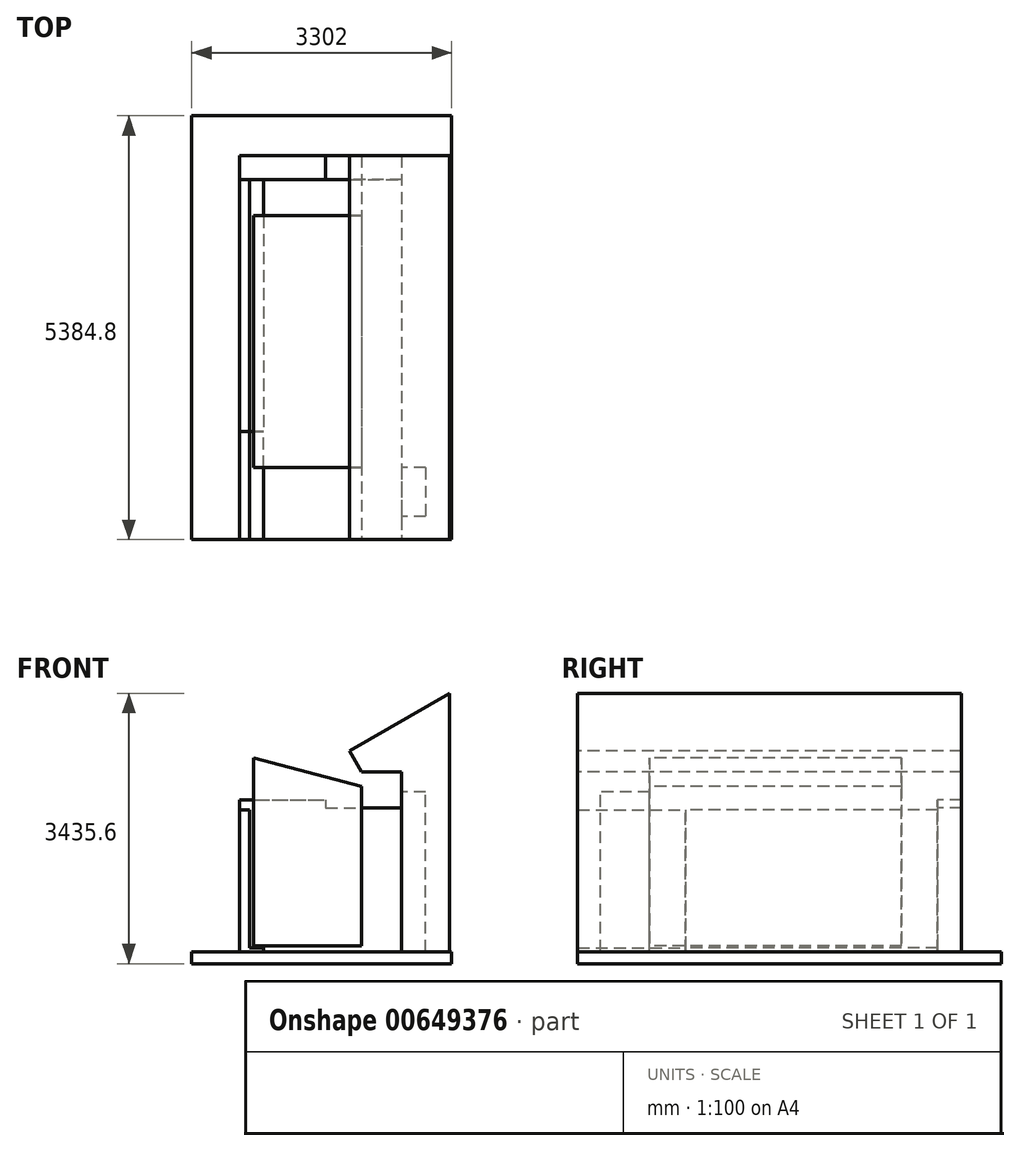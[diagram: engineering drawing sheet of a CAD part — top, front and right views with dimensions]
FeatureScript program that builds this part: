
annotation { "Feature Type Name" : "Feature", "Feature Type Description" : "" }
export const myFeature = defineFeature(function(context is Context, id is Id, definition is map)
    precondition{}
    {
        {
            var Q0;
            Q0=qCreatedBy(makeId("Front.planeOp"),FACE);
            var sketch = newSketch(context, id + "F0", { "sketchPlane" : qUnion([Q0])});
            skLineSegment(sketch, "E0", {"start": v(0, 0) * mm, "end": v(0, 1803.4) * mm});
            skLineSegment(sketch, "E1", {"start": v(0, 1803.4) * mm, "end": v(127, 1803.4) * mm});
            skLineSegment(sketch, "E2", {"start": v(127, 1803.4) * mm, "end": v(127, 50.8) * mm});
            skLineSegment(sketch, "E3", {"start": v(127, 50.8) * mm, "end": v(304.8, 50.8) * mm});
            skLineSegment(sketch, "E4", {"start": v(304.8, 50.8) * mm, "end": v(304.8, 0) * mm});
            skLineSegment(sketch, "E5", {"start": v(304.8, 0) * mm, "end": v(0, 0) * mm});
            skSolve(sketch);
        }
        {
            var Q0;
            Q0=makeQuery(id+"F0.imprint","IMPRINT",FACE,{"disambiguationData":[TD([[makeQuery(id+"F0.imprint","IMPRINT",EDGE,{"derivedFrom":sQuery(id+"F0.wireOp",EDGE,"E0")}),-1.0]])]});
            extrude(context, id + "F1", {"entities" : qUnion([Q0]), "oppositeDirection" : true, "depth" : 3200.4 * mm, "offsetDistance" : 25.4 * mm});
        }
        {
            var Q0;
            Q0=qCreatedBy(makeId("Front.planeOp"),FACE);
            var sketch = newSketch(context, id + "F2", { "sketchPlane" : qUnion([Q0])});
            skLineSegment(sketch, "E6", {"start": v(2057.4, 0) * mm, "end": v(2057.4, 2286) * mm});
            skLineSegment(sketch, "E7", {"start": v(2057.4, 2286) * mm, "end": v(1549.4, 2286) * mm});
            skLineSegment(sketch, "E8", {"start": v(1549.4, 2286) * mm, "end": v(1397, 2549.96) * mm});
            skLineSegment(sketch, "E9", {"start": v(1397, 2549.96) * mm, "end": v(2667, 3283.2) * mm});
            skLineSegment(sketch, "E10", {"start": v(2667, 3283.2) * mm, "end": v(2667, 0) * mm});
            skLineSegment(sketch, "E11", {"start": v(2667, 0) * mm, "end": v(2057.4, 0) * mm});
            skSolve(sketch);
        }
        {
            var Q0;
            Q0 = qSketchRegion(id + "F2", true);
            extrude(context, id + "F3", {"entities" : qUnion([Q0]), "oppositeDirection" : true, "depth" : 3505.2 * mm, "offsetDistance" : 25.4 * mm});
        }
        {
            var Q0;
            Q0=makeQuery(id+"F1.opExtrude","CAP_FACE",FACE,{"disambiguationData":[OSD([sQuery(id+"F0.wireOp",EDGE,"E0"),sQuery(id+"F0.wireOp",EDGE,"E1"),sQuery(id+"F0.wireOp",EDGE,"E2"),sQuery(id+"F0.wireOp",EDGE,"E3"),sQuery(id+"F0.wireOp",EDGE,"E4"),sQuery(id+"F0.wireOp",EDGE,"E5")])],"isStart":false});
            var sketch = newSketch(context, id + "F4", { "sketchPlane" : qUnion([Q0])});
            skLineSegment(sketch, "E12", {"start": v(0, 0) * mm, "end": v(0, 1930.4) * mm});
            skLineSegment(sketch, "E13", {"start": v(0, 1930.4) * mm, "end": v(-1092.2, 1930.4) * mm});
            skLineSegment(sketch, "E14", {"start": v(-1092.2, 1930.4) * mm, "end": v(-1092.2, 1828.8) * mm});
            skLineSegment(sketch, "E15", {"start": v(-1092.2, 1828.8) * mm, "end": v(-2057.4, 1828.8) * mm});
            skLineSegment(sketch, "E16", {"start": v(-2057.4, 1828.8) * mm, "end": v(-2057.4, 0) * mm});
            skLineSegment(sketch, "E17", {"start": v(-2057.4, 0) * mm, "end": v(0, 0) * mm});
            skSolve(sketch);
        }
        {
            var Q0;
            Q0 = qSketchRegion(id + "F4", true);
            extrude(context, id + "F5", {"entities" : qUnion([Q0]), "depth" : 304.8 * mm, "offsetDistance" : 25.4 * mm});
        }
        {
            var Q0;
            Q0=qCreatedBy(makeId("Front.planeOp"),FACE);
            cPlane(context, id + "F6", {"entities" : qUnion([Q0]), "cplaneType" : CPlaneType.OFFSET, "offset" : 1371.6 * mm, "width" : 152.4 * mm, "height" : 152.4 * mm});
        }
        {
            var Q0;
            Q0=makeQuery(id+"F3.opExtrude","CAP_FACE",FACE,{"disambiguationData":[OSD([sQuery(id+"F2.wireOp",EDGE,"E6"),sQuery(id+"F2.wireOp",EDGE,"E7"),sQuery(id+"F2.wireOp",EDGE,"E8"),sQuery(id+"F2.wireOp",EDGE,"E9"),sQuery(id+"F2.wireOp",EDGE,"E10"),sQuery(id+"F2.wireOp",EDGE,"E11")])],"isStart":true});
            var sketch = newSketch(context, id + "F7", { "sketchPlane" : qUnion([Q0])});
            skSolve(sketch);
        }
        {
            var Q0;
            Q0=makeQuery(id+"F7.imprint","IMPRINT",FACE,{"disambiguationData":[TD([[makeQuery(id+"F7.imprint","IMPRINT",EDGE,{"derivedFrom":makeQuery(id+"F3.opExtrude","CAP_EDGE",EDGE,{"disambiguationData":[OSD([sQuery(id+"F2.wireOp",EDGE,"E6")])],"isStart":true})}),-1.0]])]});
            var Q1;
            Q1=qCreatedBy(id+"F6.planeOp",FACE);
            extrude(context, id + "F8", {"entities" : qUnion([Q0]), "operationType" : NewBodyOperationType.ADD, "endBound" : BoundingType.UP_TO_SURFACE, "depth" : 25.4 * mm, "endBoundEntityFace" : qUnion([Q1]), "offsetDistance" : 25.4 * mm});
        }
        {
            var Q0;
            Q0=qCreatedBy(id+"F6.planeOp",FACE);
            var sketch = newSketch(context, id + "F9", { "sketchPlane" : qUnion([Q0])});
            skLineSegment(sketch, "E18.bottom", {"start": v(2692.4, 0) * mm, "end": v(-609.6, 0) * mm});
            skLineSegment(sketch, "E18.top", {"start": v(2692.4, -152.4) * mm, "end": v(-609.6, -152.4) * mm});
            skLineSegment(sketch, "E18.left", {"start": v(2692.4, 0) * mm, "end": v(2692.4, -152.4) * mm});
            skLineSegment(sketch, "E18.right", {"start": v(-609.6, 0) * mm, "end": v(-609.6, -152.4) * mm});
            skSolve(sketch);
        }
        {
            var Q0;
            Q0=makeQuery(id+"F9.imprint","IMPRINT",FACE,{"disambiguationData":[TD([[makeQuery(id+"F9.imprint","IMPRINT",EDGE,{"derivedFrom":sQuery(id+"F9.wireOp",EDGE,"E18.bottom")}),1.0]])]});
            extrude(context, id + "F10", {"entities" : qUnion([Q0]), "oppositeDirection" : true, "depth" : 5384.8 * mm, "offsetDistance" : 25.4 * mm});
        }
        {
            var Q0;
            Q0=makeQuery(id+"F1.opExtrude","CAP_FACE",FACE,{"disambiguationData":[OSD([sQuery(id+"F0.wireOp",EDGE,"E0"),sQuery(id+"F0.wireOp",EDGE,"E1"),sQuery(id+"F0.wireOp",EDGE,"E2"),sQuery(id+"F0.wireOp",EDGE,"E3"),sQuery(id+"F0.wireOp",EDGE,"E4"),sQuery(id+"F0.wireOp",EDGE,"E5")])],"isStart":true});
            var sketch = newSketch(context, id + "F11", { "sketchPlane" : qUnion([Q0])});
            skSolve(sketch);
        }
        {
            var Q0;
            Q0=makeQuery(id+"F11.imprint","IMPRINT",FACE,{"disambiguationData":[TD([[makeQuery(id+"F11.imprint","IMPRINT",EDGE,{"derivedFrom":makeQuery(id+"F1.opExtrude","CAP_EDGE",EDGE,{"disambiguationData":[OSD([sQuery(id+"F0.wireOp",EDGE,"E0")])],"isStart":true})}),-1.0]])]});
            var Q1;
            Q1=qCreatedBy(id+"F6.planeOp",FACE);
            extrude(context, id + "F12", {"entities" : qUnion([Q0]), "endBound" : BoundingType.UP_TO_SURFACE, "depth" : 25.4 * mm, "endBoundEntityFace" : qUnion([Q1]), "offsetDistance" : 25.4 * mm});
        }
        {
            var Q0;
            {var subQ0=sQuery(id+"F2.wireOp",EDGE,"E6");Q0=makeQuery(id+"F8.boolean.opBoolean","MERGE",FACE,{"derivedFrom":[makeQuery(id+"F3.opExtrude","SWEPT_FACE",FACE,{"disambiguationData":[OSD([subQ0])]}),makeQuery(id+"F8.opExtrude","SWEPT_FACE",FACE,{"disambiguationData":[OSD([subQ0])]})]});}
            var sketch = newSketch(context, id + "F13", { "sketchPlane" : qUnion([Q0])});
            skLineSegment(sketch, "E19.bottom", {"start": v(457.2, 0) * mm, "end": v(1079.5, 0) * mm});
            skLineSegment(sketch, "E19.top", {"start": v(457.2, 2032) * mm, "end": v(1079.5, 2032) * mm});
            skLineSegment(sketch, "E19.left", {"start": v(457.2, 0) * mm, "end": v(457.2, 2032) * mm});
            skLineSegment(sketch, "E19.right", {"start": v(1079.5, 0) * mm, "end": v(1079.5, 2032) * mm});
            skSolve(sketch);
        }
        {
            var Q0;
            Q0=makeQuery(id+"F13.imprint","IMPRINT",FACE,{"disambiguationData":[TD([[makeQuery(id+"F13.imprint","IMPRINT",EDGE,{"derivedFrom":sQuery(id+"F13.wireOp",EDGE,"E19.bottom")}),1.0]])]});
            extrude(context, id + "F14", {"entities" : qUnion([Q0]), "operationType" : NewBodyOperationType.REMOVE, "oppositeDirection" : true, "depth" : 304.8 * mm, "offsetDistance" : 25.4 * mm});
        }
        {
            var Q0;
            Q0=makeQuery(id+"F14.boolean.opBoolean","COPY",FACE,{"derivedFrom":makeQuery(id+"F14.opExtrude","SWEPT_FACE",FACE,{"disambiguationData":[OSD([sQuery(id+"F13.wireOp",EDGE,"E19.left")])]})});
            cPlane(context, id + "F15", {"entities" : qUnion([Q0]), "cplaneType" : CPlaneType.OFFSET, "offset" : 0 * mm, "width" : 152.4 * mm, "height" : 152.4 * mm});
        }
        {
            var Q0;
            Q0=qCreatedBy(id+"F15.planeOp",FACE);
            var sketch = newSketch(context, id + "F16", { "sketchPlane" : qUnion([Q0])});
            skLineSegment(sketch, "E20", {"start": v(177.8, 76.2) * mm, "end": v(177.8, 2463.8) * mm});
            skLineSegment(sketch, "E21", {"start": v(177.8, 2463.8) * mm, "end": v(1549.4, 2096.28) * mm});
            skLineSegment(sketch, "E22", {"start": v(1549.4, 2096.28) * mm, "end": v(1549.4, 76.2) * mm});
            skLineSegment(sketch, "E23", {"start": v(1549.4, 76.2) * mm, "end": v(177.8, 76.2) * mm});
            skSolve(sketch);
        }
        {
            var Q0;
            Q0=makeQuery(id+"F16.imprint","IMPRINT",FACE,{"disambiguationData":[TD([[makeQuery(id+"F16.imprint","IMPRINT",EDGE,{"derivedFrom":sQuery(id+"F16.wireOp",EDGE,"E20")}),-1.0]])]});
            extrude(context, id + "F17", {"entities" : qUnion([Q0]), "oppositeDirection" : true, "depth" : 3200.4 * mm, "offsetDistance" : 25.4 * mm});
        }
    });
